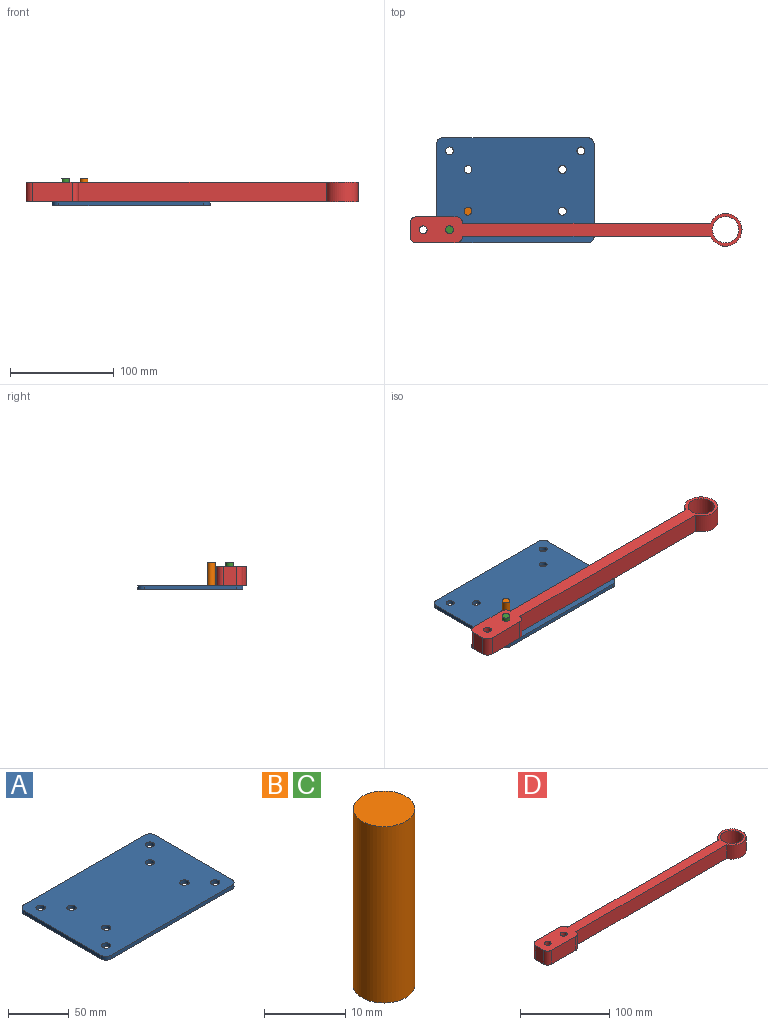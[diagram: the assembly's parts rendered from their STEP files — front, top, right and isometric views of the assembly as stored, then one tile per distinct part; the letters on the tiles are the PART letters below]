
ASSEMBLY  parts=4 mates=4
PART A: 18 faces, bbox 152.4x101.6x3.8 mm
  f0: plane 88.9x3.81mm, normal (-1,0,0), area 338.7mm2, adj f1,f15,f16,f17
  f1: cylinder r=6.35mm len=6.35mm, axis (0,0,-1), area 38mm2, adj f0,f2,f16,f17
  f2: plane 139.7x3.81mm, normal (0,-1,0), area 532.3mm2, adj f1,f3,f16,f17
  f3: cylinder r=6.35mm len=6.35mm, axis (0,0,-1), area 38mm2, adj f2,f4,f16,f17
  f4: plane 88.9x3.81mm, normal (1,0,0), area 338.7mm2, adj f3,f5,f16,f17
  f5: cylinder r=6.35mm len=6.35mm, axis (0,0,-1), area 38mm2, adj f4,f6,f16,f17
  f6: plane 139.7x3.81mm, normal (0,1,0), area 532.3mm2, adj f5,f15,f16,f17
  f7: cylinder r=3.81mm len=7.62mm, axis (0,0,-1), area 91.2mm2, adj f16,f17
  f8: cylinder r=3.81mm len=7.62mm, axis (0,0,-1), area 91.2mm2, adj f16,f17
  f9: cylinder r=3.81mm len=7.62mm, axis (0,0,-1), area 91.2mm2, adj f16,f17
  f10: cylinder r=3.81mm len=7.62mm, axis (0,0,-1), area 91.2mm2, adj f16,f17
  f11: cylinder r=3.81mm len=7.62mm, axis (0,0,-1), area 91.2mm2, adj f16,f17
  f12: cylinder r=3.81mm len=7.62mm, axis (0,0,-1), area 91.2mm2, adj f16,f17
  f13: cylinder r=3.81mm len=7.62mm, axis (0,0,-1), area 91.2mm2, adj f16,f17
  f14: cylinder r=3.81mm len=7.62mm, axis (0,0,-1), area 91.2mm2, adj f16,f17
  f15: cylinder r=6.35mm len=6.35mm, axis (0,0,-1), area 38mm2, adj f0,f6,f16,f17
  f16: plane 152.4x101.6mm, normal (0,0,1), area 15084.4mm2, adj f0,f1,f2,f3,f4,f5,f6,f7
  f17: plane 152.4x101.6mm, normal (0,0,-1), area 15084.4mm2, adj f0,f1,f2,f3,f4,f5,f6,f7
PART B: 3 faces, bbox 7.6x7.6x26.7 mm
  f0: cylinder r=3.81mm len=26.67mm, axis (0,0,-1), area 638.5mm2, adj f1,f2
  f1: plane 7.62x7.62mm, normal (0,0,1), area 45.6mm2, adj f0
  f2: plane 7.62x7.62mm, normal (0,0,-1), area 45.6mm2, adj f0
PART C: same geometry as B
PART D: 15 faces, bbox 320.7x31.8x19.1 mm
  f0: plane 239.45x19.05mm, normal (0,1,0), area 4561.5mm2, adj f1,f11,f13,f14
  f1: cylinder r=6.35mm len=19.05mm, axis (0,0,-1), area 190mm2, adj f0,f2,f13,f14
  f2: plane 38.1x19.05mm, normal (0,1,0), area 725.8mm2, adj f1,f3,f13,f14
  f3: cylinder r=6.35mm len=19.05mm, axis (0,0,-1), area 190mm2, adj f2,f4,f13,f14
  f4: plane 19.05x12.7mm, normal (-1,0,0), area 241.9mm2, adj f3,f5,f13,f14
  f5: cylinder r=6.35mm len=19.05mm, axis (0,0,-1), area 190mm2, adj f4,f6,f13,f14
  f6: plane 38.1x19.05mm, normal (0,-1,0), area 725.8mm2, adj f5,f7,f13,f14
  f7: cylinder r=6.35mm len=19.05mm, axis (0,0,-1), area 190mm2, adj f6,f8,f13,f14
  f8: plane 239.45x19.05mm, normal (0,-1,0), area 4561.5mm2, adj f7,f11,f13,f14
  f9: cylinder r=3.81mm len=19.05mm, axis (0,0,-1), area 456mm2, adj f13,f14
  f10: cylinder r=12.7mm len=25.4mm, axis (0,0,-1), area 1520.1mm2, adj f13,f14
  f11: cylinder r=15.88mm len=31.75mm, axis (0,0,-1), area 1651.3mm2, adj f0,f8,f13,f14
  f12: cylinder r=3.81mm len=19.05mm, axis (0,0,-1), area 456mm2, adj f13,f14
  f13: plane 320.68x31.75mm, normal (0,0,1), area 4479.2mm2, adj f0,f1,f2,f3,f4,f5,f6,f7
  f14: plane 320.68x31.75mm, normal (0,0,-1), area 4479.2mm2, adj f0,f1,f2,f3,f4,f5,f6,f7
PLACE A t=(3.88,14.8,-12.31)mm
PLACE B t=(-24.05,-51.73,-12.31)mm
PLACE C t=(-42.01,-69.7,-12.31)mm
PLACE D t=(59.34,-58.62,-8.5)mm
MATE fastened B.f0 <-> A.f14  axis (0,0,-1) through (-47.93,-21.78,-12.31)mm
MATE fastened D.f9 <-> A.f14  axis (0,0,-1) through (-91.29,-39.74,-8.5)mm
MATE fastened D.f12 <-> A.f9  axis (0,0,-1) through (-65.89,-39.74,-8.5)mm
MATE fastened C.f0 <-> A.f9  axis (0,0,-1) through (-65.89,-39.74,-12.31)mm
